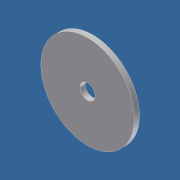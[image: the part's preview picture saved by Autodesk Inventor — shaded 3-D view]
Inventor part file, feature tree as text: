
AUTODESK INVENTOR PART (.ipt)
format: ipt  version: 2012 (Build 160160000, 160)  size: 70,656 bytes
history: native  units: in
note: dims shown in document units (in); Inventor stores cm internally (conversion verified against a paired STEP export)
features: extrude x1, sketch x1
ambient origin geometry x8: Origin, YZ Plane, XZ Plane, XY Plane, X Axis, Y Axis, Z Axis, Center Point
bodies: Solid1 (feature_tree)
feature tree (2):
  extrude  "Extrusion1"  Depth=1.25in
  sketch  "Sketch1"  dims[d0=0.203in d1=1.25in d2=0.07in d3=0.0in]
